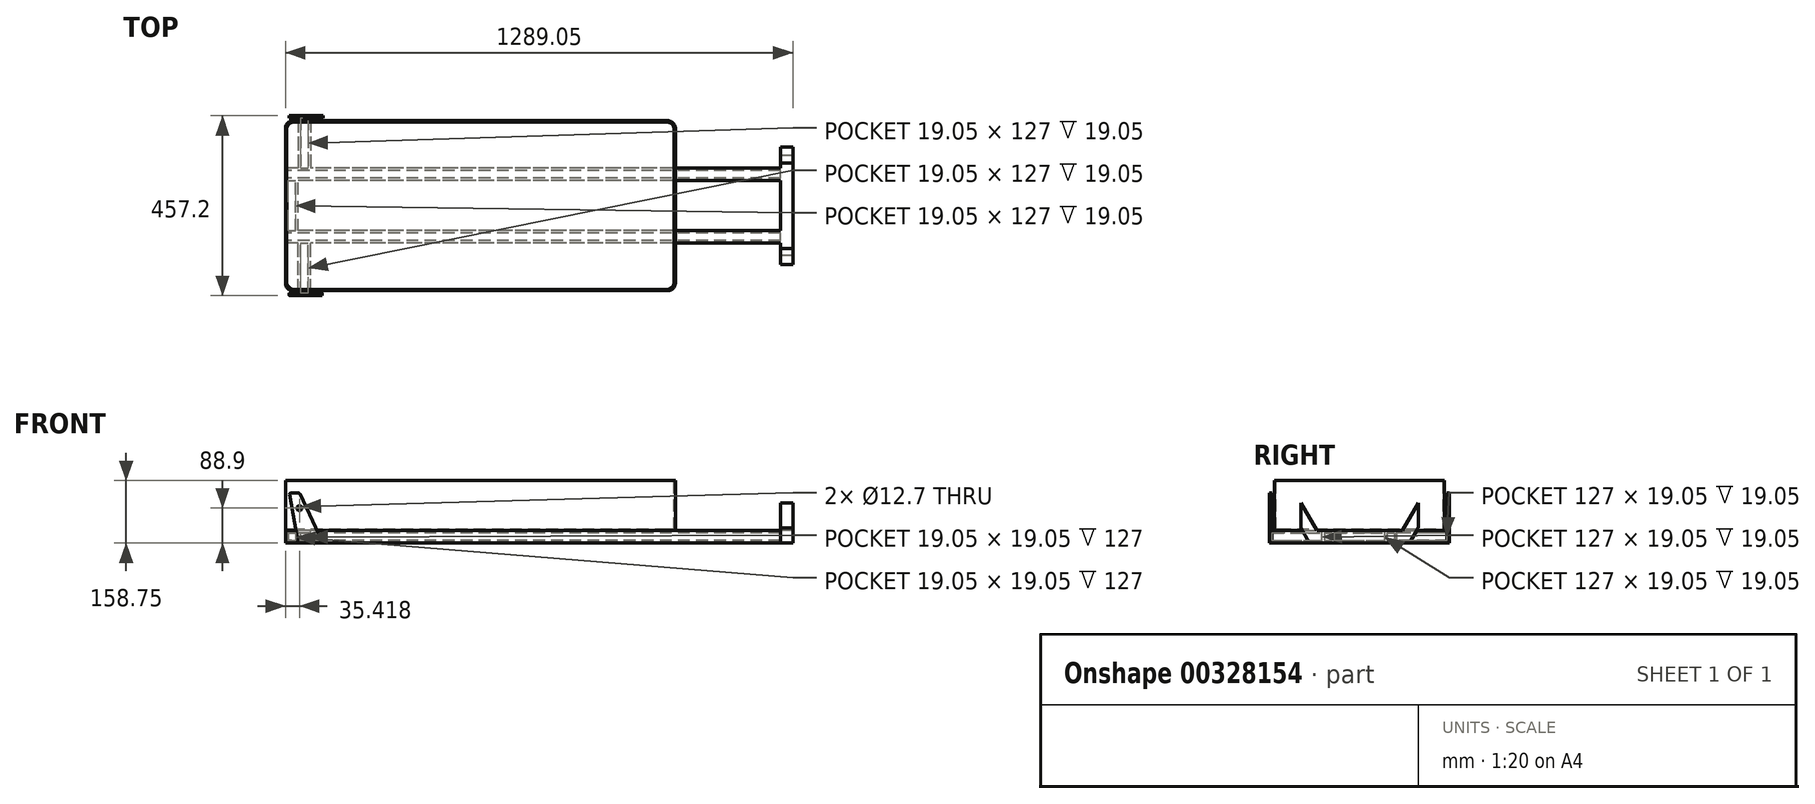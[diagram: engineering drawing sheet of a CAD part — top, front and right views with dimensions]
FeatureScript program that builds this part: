
annotation { "Feature Type Name" : "Feature", "Feature Type Description" : "" }
export const myFeature = defineFeature(function(context is Context, id is Id, definition is map)
    precondition{}
    {
        {
            var Q0;
            Q0=qCreatedBy(makeId("Front.planeOp"),FACE);
            var sketch = newSketch(context, id + "F0", { "sketchPlane" : qUnion([Q0])});
            skLineSegment(sketch, "E0.bottom", {"start": v(495.3, 63.5) * mm, "end": v(-495.3, 63.5) * mm});
            skLineSegment(sketch, "E0.top", {"start": v(495.3, -63.5) * mm, "end": v(-495.3, -63.5) * mm});
            skLineSegment(sketch, "E0.left", {"start": v(495.3, 63.5) * mm, "end": v(495.3, -63.5) * mm});
            skLineSegment(sketch, "E0.right", {"start": v(-495.3, 63.5) * mm, "end": v(-495.3, -63.5) * mm});
            skPoint(sketch, "E0.middle", {"position": v(0, 0) * mm});
            skSolve(sketch);
        }
        {
            var Q0;
            Q0 = qSketchRegion(id + "F0", true);
            extrude(context, id + "F1", {"entities" : qUnion([Q0]), "depth" : 431.8 * mm});
        }
        {
            var Q0;
            Q0=makeQuery(id+"F1.opExtrude","CAP_EDGE",EDGE,{"disambiguationData":[OSD([sQuery(id+"F0.wireOp",EDGE,"E0.left")])],"isStart":false});
            var Q1;
            Q1=makeQuery(id+"F1.opExtrude","CAP_EDGE",EDGE,{"disambiguationData":[OSD([sQuery(id+"F0.wireOp",EDGE,"E0.left")])],"isStart":true});
            var Q2;
            Q2=makeQuery(id+"F1.opExtrude","CAP_EDGE",EDGE,{"disambiguationData":[OSD([sQuery(id+"F0.wireOp",EDGE,"E0.right")])],"isStart":false});
            var Q3;
            Q3=makeQuery(id+"F1.opExtrude","CAP_EDGE",EDGE,{"disambiguationData":[OSD([sQuery(id+"F0.wireOp",EDGE,"E0.right")])],"isStart":true});
            fillet(context, id + "F2", {"entities" : qUnion([Q0, Q1, Q2, Q3]), "radius" : 19.05 * mm, "tangentPropagation" : true, "allowEdgeOverflow" : false});
        }
        {
            var Q0;
            Q0=makeQuery(id+"F1.opExtrude","SWEPT_FACE",FACE,{"disambiguationData":[OSD([sQuery(id+"F0.wireOp",EDGE,"E0.bottom")])]});
            var sketch = newSketch(context, id + "F3", { "sketchPlane" : qUnion([Q0])});
            skLineSegment(sketch, "E1.bottom", {"start": v(473.08, -3.18) * mm, "end": v(-473.08, -3.18) * mm});
            skLineSegment(sketch, "E1.top", {"start": v(473.08, -428.63) * mm, "end": v(-473.08, -428.63) * mm});
            skLineSegment(sketch, "E1.left", {"start": v(492.13, -22.23) * mm, "end": v(492.13, -409.58) * mm});
            skLineSegment(sketch, "E1.right", {"start": v(-492.13, -22.23) * mm, "end": v(-492.13, -409.58) * mm});
            skPoint(sketch, "E1.middle", {"position": v(0, -215.9) * mm});
            skPoint(sketch, "E2.visualSharp", {"position": v(-492.13, -3.18) * mm});
            skArc(sketch, "E2.filletArc", {"start": v(-473.08, -3.18) * mm, "mid": v(-486.55, -8.75) * mm, "end": v(-492.13, -22.22) * mm});
            skPoint(sketch, "E3.visualSharp", {"position": v(492.13, -3.18) * mm});
            skArc(sketch, "E3.filletArc", {"start": v(492.13, -22.23) * mm, "mid": v(486.55, -8.75) * mm, "end": v(473.08, -3.18) * mm});
            skPoint(sketch, "E4.visualSharp", {"position": v(492.13, -428.63) * mm});
            skArc(sketch, "E4.filletArc", {"start": v(473.08, -428.63) * mm, "mid": v(486.55, -423.05) * mm, "end": v(492.13, -409.58) * mm});
            skPoint(sketch, "E5.visualSharp", {"position": v(-492.13, -428.63) * mm});
            skArc(sketch, "E5.filletArc", {"start": v(-492.13, -409.58) * mm, "mid": v(-486.55, -423.05) * mm, "end": v(-473.08, -428.63) * mm});
            skSolve(sketch);
        }
        {
            var Q0;
            Q0 = qSketchRegion(id + "F3", true);
            extrude(context, id + "F4", {"entities" : qUnion([Q0]), "operationType" : NewBodyOperationType.REMOVE, "oppositeDirection" : true, "depth" : 123.82 * mm});
        }
        {
            var Q0;
            Q0=qCreatedBy(makeId("Right.planeOp"),FACE);
            var sketch = newSketch(context, id + "F5", { "sketchPlane" : qUnion([Q0])});
            skLineSegment(sketch, "E6.bottom", {"start": v(-311.15, -63.5) * mm, "end": v(-279.4, -63.5) * mm});
            skLineSegment(sketch, "E6.top", {"start": v(-311.15, -95.25) * mm, "end": v(-279.4, -95.25) * mm});
            skLineSegment(sketch, "E6.left", {"start": v(-311.15, -63.5) * mm, "end": v(-311.15, -95.25) * mm});
            skLineSegment(sketch, "E6.right", {"start": v(-279.4, -63.5) * mm, "end": v(-279.4, -95.25) * mm});
            skLineSegment(sketch, "E7.bottom", {"start": v(-152.4, -63.5) * mm, "end": v(-120.65, -63.5) * mm});
            skLineSegment(sketch, "E7.top", {"start": v(-152.4, -95.25) * mm, "end": v(-120.65, -95.25) * mm});
            skLineSegment(sketch, "E7.left", {"start": v(-152.4, -63.5) * mm, "end": v(-152.4, -95.25) * mm});
            skLineSegment(sketch, "E7.right", {"start": v(-120.65, -63.5) * mm, "end": v(-120.65, -95.25) * mm});
            skLineSegment(sketch, "E8", {"start": v(-215.9, 65.63) * mm, "end": v(-215.9, -63.07) * mm, "construction": true});
            skLineSegment(sketch, "E9.0", {"start": v(-304.8, -88.9) * mm, "end": v(-285.75, -88.9) * mm});
            skLineSegment(sketch, "E9.1", {"start": v(-304.8, -69.85) * mm, "end": v(-304.8, -88.9) * mm});
            skLineSegment(sketch, "E9.2", {"start": v(-304.8, -69.85) * mm, "end": v(-285.75, -69.85) * mm});
            skLineSegment(sketch, "E9.3", {"start": v(-285.75, -69.85) * mm, "end": v(-285.75, -88.9) * mm});
            skLineSegment(sketch, "E10.0", {"start": v(-146.05, -69.85) * mm, "end": v(-146.05, -88.9) * mm});
            skLineSegment(sketch, "E10.1", {"start": v(-146.05, -69.85) * mm, "end": v(-127, -69.85) * mm});
            skLineSegment(sketch, "E10.2", {"start": v(-127, -69.85) * mm, "end": v(-127, -88.9) * mm});
            skLineSegment(sketch, "E10.3", {"start": v(-146.05, -88.9) * mm, "end": v(-127, -88.9) * mm});
            skSolve(sketch);
        }
        {
            var Q0;
            Q0 = qSketchRegion(id + "F5", true);
            extrude(context, id + "F6", {"entities" : qUnion([Q0]), "operationType" : NewBodyOperationType.ADD, "depth" : 762 * mm, "hasSecondDirection" : true, "secondDirectionOppositeDirection" : true, "secondDirectionDepth" : 495.3 * mm});
        }
        {
            var Q0;
            Q0=makeQuery(id+"F6.opExtrude","SWEPT_FACE",FACE,{"disambiguationData":[OSD([sQuery(id+"F5.wireOp",EDGE,"E7.left")])]});
            var sketch = newSketch(context, id + "F7", { "sketchPlane" : qUnion([Q0])});
            skLineSegment(sketch, "E11.bottom", {"start": v(-495.3, -63.5) * mm, "end": v(-463.55, -63.5) * mm});
            skLineSegment(sketch, "E11.top", {"start": v(-495.3, -95.25) * mm, "end": v(-463.55, -95.25) * mm});
            skLineSegment(sketch, "E11.left", {"start": v(-495.3, -63.5) * mm, "end": v(-495.3, -95.25) * mm});
            skLineSegment(sketch, "E11.right", {"start": v(-463.55, -63.5) * mm, "end": v(-463.55, -95.25) * mm});
            skLineSegment(sketch, "E12.0", {"start": v(-488.95, -88.9) * mm, "end": v(-469.9, -88.9) * mm});
            skLineSegment(sketch, "E12.1", {"start": v(-488.95, -69.85) * mm, "end": v(-488.95, -88.9) * mm});
            skLineSegment(sketch, "E12.2", {"start": v(-488.95, -69.85) * mm, "end": v(-469.9, -69.85) * mm});
            skLineSegment(sketch, "E12.3", {"start": v(-469.9, -69.85) * mm, "end": v(-469.9, -88.9) * mm});
            skSolve(sketch);
        }
        {
            var Q0;
            Q0 = qSketchRegion(id + "F7", true);
            extrude(context, id + "F8", {"entities" : qUnion([Q0]), "operationType" : NewBodyOperationType.ADD, "depth" : 127 * mm});
        }
        {
            var Q0;
            Q0=makeQuery(id+"F6.opExtrude","SWEPT_FACE",FACE,{"disambiguationData":[OSD([sQuery(id+"F5.wireOp",EDGE,"E6.left")])]});
            var sketch = newSketch(context, id + "F9", { "sketchPlane" : qUnion([Q0])});
            skSolve(sketch);
        }
        {
            var Q0;
            {var subQ1=sQuery(id+"F5.wireOp",EDGE,"E6.left");Q0=makeQuery(id+"F9.imprint","IMPRINT",FACE,{"disambiguationData":[TD([[makeQuery(id+"F9.imprint","IMPRINT",EDGE,{"derivedFrom":makeQuery(id+"F6.opExtrude","CAP_EDGE",EDGE,{"disambiguationData":[OSD([subQ1])],"isStart":true})}),1.0]])]});}
            var sketch = newSketch(context, id + "F10", { "sketchPlane" : qUnion([Q0])});
            skLineSegment(sketch, "E13.bottom", {"start": v(-463.55, -95.25) * mm, "end": v(-431.8, -95.25) * mm});
            skLineSegment(sketch, "E13.top", {"start": v(-463.55, -63.5) * mm, "end": v(-431.8, -63.5) * mm});
            skLineSegment(sketch, "E13.left", {"start": v(-463.55, -95.25) * mm, "end": v(-463.55, -63.5) * mm});
            skLineSegment(sketch, "E13.right", {"start": v(-431.8, -95.25) * mm, "end": v(-431.8, -63.5) * mm});
            skLineSegment(sketch, "E14.0", {"start": v(-457.2, -88.9) * mm, "end": v(-457.2, -69.85) * mm});
            skLineSegment(sketch, "E14.1", {"start": v(-457.2, -88.9) * mm, "end": v(-438.15, -88.9) * mm});
            skLineSegment(sketch, "E14.2", {"start": v(-438.15, -88.9) * mm, "end": v(-438.15, -69.85) * mm});
            skLineSegment(sketch, "E14.3", {"start": v(-457.2, -69.85) * mm, "end": v(-438.15, -69.85) * mm});
            skSolve(sketch);
        }
        {
            var Q0;
            Q0 = qSketchRegion(id + "F10", true);
            extrude(context, id + "F11", {"entities" : qUnion([Q0]), "operationType" : NewBodyOperationType.ADD, "depth" : 127 * mm});
        }
        {
            var Q0;
            Q0=makeQuery(id+"F6.opExtrude","SWEPT_FACE",FACE,{"disambiguationData":[OSD([sQuery(id+"F5.wireOp",EDGE,"E7.right")])]});
            var sketch = newSketch(context, id + "F12", { "sketchPlane" : qUnion([Q0])});
            skLineSegment(sketch, "E15.bottom", {"start": v(463.55, -95.25) * mm, "end": v(431.8, -95.25) * mm});
            skLineSegment(sketch, "E15.top", {"start": v(463.55, -63.5) * mm, "end": v(431.8, -63.5) * mm});
            skLineSegment(sketch, "E15.left", {"start": v(463.55, -95.25) * mm, "end": v(463.55, -63.5) * mm});
            skLineSegment(sketch, "E15.right", {"start": v(431.8, -95.25) * mm, "end": v(431.8, -63.5) * mm});
            skLineSegment(sketch, "E16.0", {"start": v(457.2, -88.9) * mm, "end": v(457.2, -69.85) * mm});
            skLineSegment(sketch, "E16.1", {"start": v(457.2, -88.9) * mm, "end": v(438.15, -88.9) * mm});
            skLineSegment(sketch, "E16.2", {"start": v(438.15, -88.9) * mm, "end": v(438.15, -69.85) * mm});
            skLineSegment(sketch, "E16.3", {"start": v(457.2, -69.85) * mm, "end": v(438.15, -69.85) * mm});
            skSolve(sketch);
        }
        {
            var Q0;
            Q0 = qSketchRegion(id + "F12", true);
            extrude(context, id + "F13", {"entities" : qUnion([Q0]), "operationType" : NewBodyOperationType.ADD, "depth" : 127 * mm});
        }
        {
            var Q0;
            Q0=makeQuery(id+"F11.opExtrude","CAP_FACE",FACE,{"disambiguationData":[OSD([sQuery(id+"F10.wireOp",EDGE,"E13.bottom"),sQuery(id+"F10.wireOp",EDGE,"E13.top"),sQuery(id+"F10.wireOp",EDGE,"E13.left"),sQuery(id+"F10.wireOp",EDGE,"E13.right"),sQuery(id+"F10.wireOp",EDGE,"E14.0"),sQuery(id+"F10.wireOp",EDGE,"E14.1"),sQuery(id+"F10.wireOp",EDGE,"E14.2"),sQuery(id+"F10.wireOp",EDGE,"E14.3")])],"isStart":false});
            cPlane(context, id + "F14", {"entities" : qUnion([Q0]), "cplaneType" : CPlaneType.OFFSET, "offset" : 0 * mm, "width" : 152.4 * mm, "height" : 152.4 * mm});
        }
        {
            var Q0;
            Q0=qCreatedBy(id+"F14.planeOp",FACE);
            var sketch = newSketch(context, id + "F15", { "sketchPlane" : qUnion([Q0])});
            skLineSegment(sketch, "E17", {"start": v(-463.55, -95.25) * mm, "end": v(-485.29, 28.02) * mm});
            skLineSegment(sketch, "E18", {"start": v(-482.16, 31.75) * mm, "end": v(-461.3, 31.75) * mm});
            skLineSegment(sketch, "E19", {"start": v(-458.42, 29.92) * mm, "end": v(-402.16, -90.73) * mm});
            skLineSegment(sketch, "E20", {"start": v(-405.03, -95.25) * mm, "end": v(-463.55, -95.25) * mm});
            skPoint(sketch, "E21.visualSharp", {"position": v(-485.94, 31.75) * mm});
            skArc(sketch, "E21.filletArc", {"start": v(-482.16, 31.75) * mm, "mid": v(-484.6, 30.62) * mm, "end": v(-485.29, 28.02) * mm});
            skPoint(sketch, "E22.visualSharp", {"position": v(-459.27, 31.75) * mm});
            skArc(sketch, "E22.filletArc", {"start": v(-458.42, 29.92) * mm, "mid": v(-459.59, 31.25) * mm, "end": v(-461.3, 31.75) * mm});
            skPoint(sketch, "E23.visualSharp", {"position": v(-400.05, -95.25) * mm});
            skArc(sketch, "E23.filletArc", {"start": v(-405.03, -95.25) * mm, "mid": v(-402.36, -93.78) * mm, "end": v(-402.16, -90.73) * mm});
            skCircle(sketch, "E24", {"center": v(-459.88, -6.35) * mm, "radius": 6.35 * mm});
            skSolve(sketch);
        }
        {
            var Q0;
            Q0 = qSketchRegion(id + "F15", true);
            extrude(context, id + "F16", {"entities" : qUnion([Q0]), "operationType" : NewBodyOperationType.ADD, "depth" : 6.35 * mm});
        }
        {
            var Q0;
            Q0=makeQuery(id+"F13.opExtrude","CAP_FACE",FACE,{"disambiguationData":[OSD([sQuery(id+"F12.wireOp",EDGE,"E15.bottom"),sQuery(id+"F12.wireOp",EDGE,"E15.top"),sQuery(id+"F12.wireOp",EDGE,"E15.left"),sQuery(id+"F12.wireOp",EDGE,"E15.right"),sQuery(id+"F12.wireOp",EDGE,"E16.0"),sQuery(id+"F12.wireOp",EDGE,"E16.1"),sQuery(id+"F12.wireOp",EDGE,"E16.2"),sQuery(id+"F12.wireOp",EDGE,"E16.3")])],"isStart":false});
            cPlane(context, id + "F17", {"entities" : qUnion([Q0]), "cplaneType" : CPlaneType.OFFSET, "offset" : 0 * mm, "width" : 152.4 * mm, "height" : 152.4 * mm});
        }
        {
            var Q0;
            Q0=qCreatedBy(id+"F17.planeOp",FACE);
            var sketch = newSketch(context, id + "F18", { "sketchPlane" : qUnion([Q0])});
            skLineSegment(sketch, "E25", {"start": v(463.55, -95.25) * mm, "end": v(485.94, 31.75) * mm});
            skLineSegment(sketch, "E26", {"start": v(459.27, 31.75) * mm, "end": v(400.05, -95.25) * mm});
            skLineSegment(sketch, "E27", {"start": v(400.05, -95.25) * mm, "end": v(463.55, -95.25) * mm});
            skLineSegment(sketch, "E28", {"start": v(459.27, 31.75) * mm, "end": v(485.94, 31.75) * mm});
            skCircle(sketch, "E29", {"center": v(459.88, -6.35) * mm, "radius": 6.35 * mm});
            skSolve(sketch);
        }
        {
            var Q0;
            Q0=makeQuery(id+"F18.imprint","IMPRINT",FACE,{"disambiguationData":[TD([[makeQuery(id+"F18.imprint","IMPRINT",EDGE,{"derivedFrom":sQuery(id+"F18.wireOp",EDGE,"E25")}),1.0]])]});
            extrude(context, id + "F19", {"entities" : qUnion([Q0]), "operationType" : NewBodyOperationType.ADD, "depth" : 6.35 * mm});
        }
        {
            var Q0;
            Q0=makeQuery(id+"F6.opExtrude","CAP_FACE",FACE,{"disambiguationData":[OSD([sQuery(id+"F5.wireOp",EDGE,"E6.bottom"),sQuery(id+"F5.wireOp",EDGE,"E6.top"),sQuery(id+"F5.wireOp",EDGE,"E6.left"),sQuery(id+"F5.wireOp",EDGE,"E6.right"),sQuery(id+"F5.wireOp",EDGE,"E9.0"),sQuery(id+"F5.wireOp",EDGE,"E9.1"),sQuery(id+"F5.wireOp",EDGE,"E9.2"),sQuery(id+"F5.wireOp",EDGE,"E9.3")])],"isStart":false});
            cPlane(context, id + "F20", {"entities" : qUnion([Q0]), "cplaneType" : CPlaneType.OFFSET, "offset" : 0 * mm, "width" : 152.4 * mm, "height" : 152.4 * mm});
        }
        {
            var Q0;
            Q0=qCreatedBy(id+"F20.planeOp",FACE);
            var sketch = newSketch(context, id + "F21", { "sketchPlane" : qUnion([Q0])});
            skLineSegment(sketch, "E30", {"start": v(-364.9, 6.35) * mm, "end": v(-364.9, -57.15) * mm});
            skLineSegment(sketch, "E31", {"start": v(-364.9, -57.15) * mm, "end": v(-342.9, -95.25) * mm});
            skLineSegment(sketch, "E32", {"start": v(-342.9, -95.25) * mm, "end": v(-88.9, -95.25) * mm});
            skLineSegment(sketch, "E33", {"start": v(-88.9, -95.25) * mm, "end": v(-66.9, -57.15) * mm});
            skLineSegment(sketch, "E34", {"start": v(-66.9, -57.15) * mm, "end": v(-66.9, 6.35) * mm});
            skLineSegment(sketch, "E35", {"start": v(-66.9, 6.35) * mm, "end": v(-107.23, -63.5) * mm});
            skLineSegment(sketch, "E36", {"start": v(-107.23, -63.5) * mm, "end": v(-324.57, -63.5) * mm});
            skLineSegment(sketch, "E37", {"start": v(-324.57, -63.5) * mm, "end": v(-364.9, 6.35) * mm});
            skLineSegment(sketch, "E38", {"start": v(-215.9, 63.08) * mm, "end": v(-215.9, 0) * mm, "construction": true});
            skSolve(sketch);
        }
        {
            var Q0;
            Q0=makeQuery(id+"F21.imprint","IMPRINT",FACE,{"disambiguationData":[TD([[makeQuery(id+"F21.imprint","IMPRINT",EDGE,{"derivedFrom":sQuery(id+"F21.wireOp",EDGE,"E30")}),1.0]])]});
            extrude(context, id + "F22", {"entities" : qUnion([Q0]), "operationType" : NewBodyOperationType.ADD, "depth" : 31.75 * mm});
        }
    });
